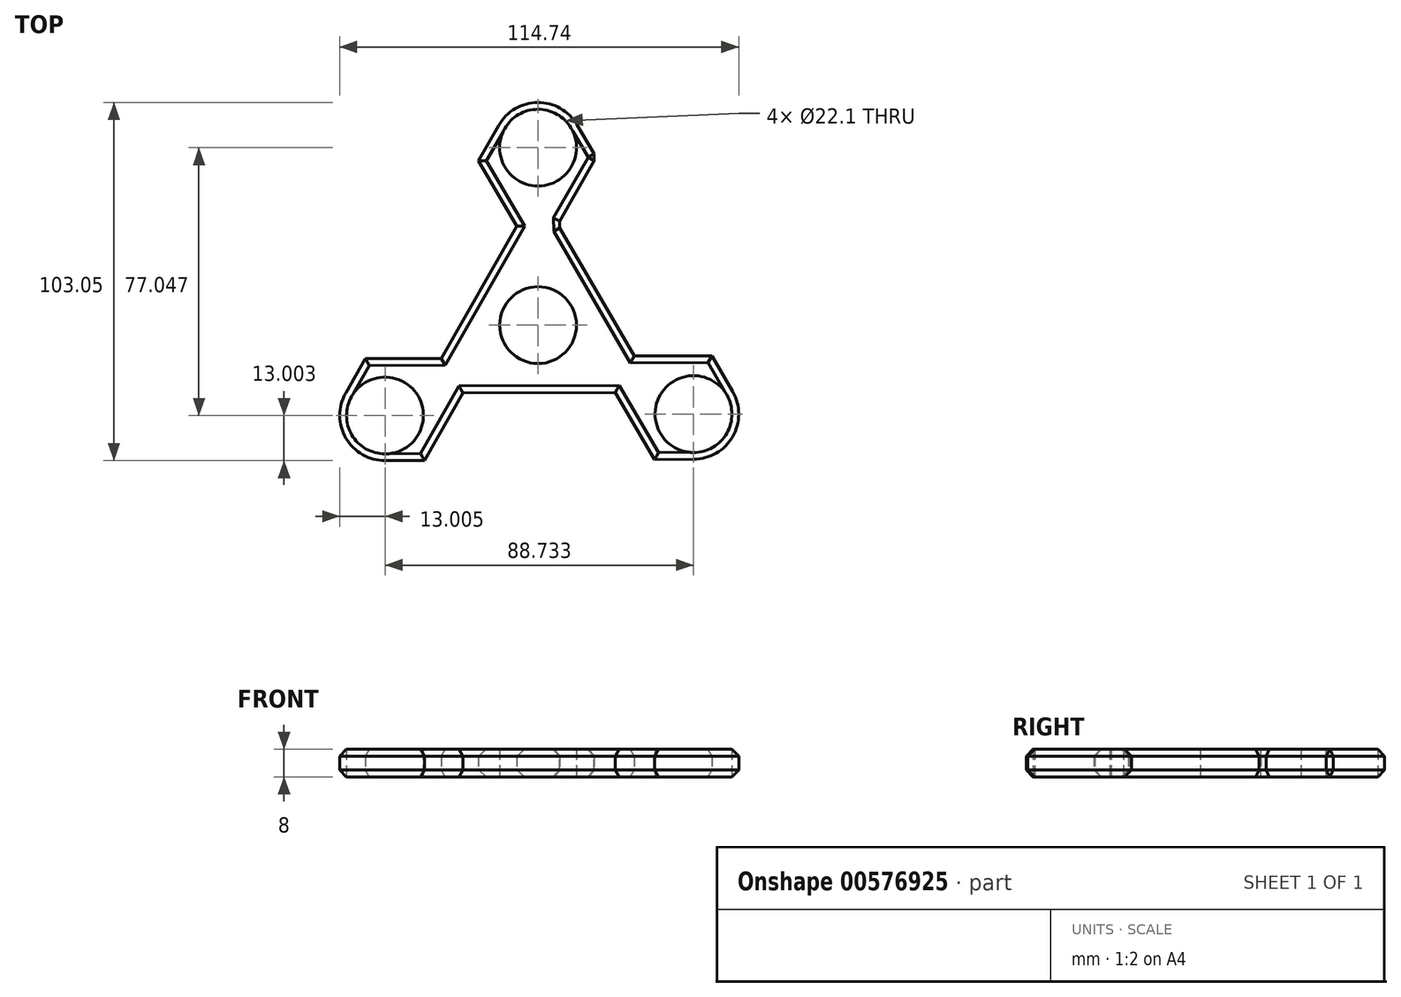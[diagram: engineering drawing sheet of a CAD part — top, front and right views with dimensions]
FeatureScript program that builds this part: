
annotation { "Feature Type Name" : "Feature", "Feature Type Description" : "" }
export const myFeature = defineFeature(function(context is Context, id is Id, definition is map)
    precondition{}
    {
        {
            var Q0;
            Q0=qCreatedBy(makeId("Top.planeOp"),FACE);
            var sketch = newSketch(context, id + "F0", { "sketchPlane" : qUnion([Q0])});
            skCircle(sketch, "E0", {"center": v(0, 0) * mm, "radius": 11.05 * mm});
            skCircle(sketch, "E1", {"center": v(0, 51.05) * mm, "radius": 13 * mm});
            skCircle(sketch, "E2.1.0", {"center": v(-44.02, -26) * mm, "radius": 13 * mm});
            skCircle(sketch, "E2.2.0", {"center": v(44.72, -25.6) * mm, "radius": 13 * mm});
            skPoint(sketch, "E2.center", {"position": v(0.23, -0.18) * mm});
            skLineSegment(sketch, "E3", {"start": v(-55.3, -19.55) * mm, "end": v(-49.66, -9.67) * mm});
            skLineSegment(sketch, "E4", {"start": v(-43.96, -39) * mm, "end": v(-32.66, -38.95) * mm});
            skLineSegment(sketch, "E5", {"start": v(-32.66, -38.95) * mm, "end": v(-21.58, -19.55) * mm});
            skLineSegment(sketch, "E6", {"start": v(-21.58, -19.55) * mm, "end": v(22.22, -19.35) * mm});
            skLineSegment(sketch, "E7", {"start": v(22.22, -19.35) * mm, "end": v(33.48, -38.64) * mm});
            skLineSegment(sketch, "E8.1.0", {"start": v(50.06, -8.8) * mm, "end": v(27.72, -8.91) * mm});
            skLineSegment(sketch, "E8.1.1", {"start": v(27.72, -8.91) * mm, "end": v(5.65, 28.92) * mm});
            skLineSegment(sketch, "E8.1.2", {"start": v(5.65, 28.92) * mm, "end": v(16.73, 48.31) * mm});
            skLineSegment(sketch, "E8.2.0", {"start": v(-17.4, 47.75) * mm, "end": v(-6.14, 28.46) * mm});
            skLineSegment(sketch, "E8.2.1", {"start": v(-6.14, 28.46) * mm, "end": v(-27.87, -9.57) * mm});
            skLineSegment(sketch, "E8.2.2", {"start": v(-27.87, -9.57) * mm, "end": v(-50.2, -9.67) * mm});
            skLineSegment(sketch, "E9.trimOffspring", {"start": v(33.48, -38.64) * mm, "end": v(44.78, -38.6) * mm});
            skLineSegment(sketch, "E10.trimOffspring", {"start": v(-17.12, 47.28) * mm, "end": v(-11.29, 57.5) * mm});
            skLineSegment(sketch, "E11", {"start": v(16.73, 48.31) * mm, "end": v(11.19, 57.67) * mm});
            skLineSegment(sketch, "E12", {"start": v(50.06, -8.8) * mm, "end": v(55.98, -19.1) * mm});
            skCircle(sketch, "E13", {"center": v(0, 51.05) * mm, "radius": 11.05 * mm});
            skCircle(sketch, "E14.1.0", {"center": v(-44.02, -26) * mm, "radius": 11.05 * mm});
            skCircle(sketch, "E14.2.0", {"center": v(44.72, -25.6) * mm, "radius": 11.05 * mm});
            skSolve(sketch);
        }
        {
            var Q0;
            Q0 = qSketchRegion(id + "F0", true);
            extrude(context, id + "F1", {"entities" : qUnion([Q0]), "depth" : 8 * mm, "offsetDistance" : 25 * mm});
        }
        {
            var Q0;
            Q0=makeQuery(id+"F1.opExtrude","CAP_EDGE",EDGE,{"disambiguationData":[OSD([sQuery(id+"F0.wireOp",EDGE,"E8.1.1")])],"isStart":false});
            var Q1;
            Q1=makeQuery(id+"F1.opExtrude","CAP_EDGE",EDGE,{"disambiguationData":[OSD([sQuery(id+"F0.wireOp",EDGE,"E8.1.2")])],"isStart":false});
            var Q2;
            Q2=makeQuery(id+"F1.opExtrude","CAP_EDGE",EDGE,{"disambiguationData":[OSD([sQuery(id+"F0.wireOp",EDGE,"E11")])],"isStart":false});
            var Q3;
            Q3=makeQuery(id+"F1.opExtrude","CAP_EDGE",EDGE,{"disambiguationData":[OSD([sQuery(id+"F0.wireOp",EDGE,"E8.2.0")])],"isStart":false});
            var Q4;
            Q4=makeQuery(id+"F1.opExtrude","CAP_EDGE",EDGE,{"disambiguationData":[OSD([sQuery(id+"F0.wireOp",EDGE,"E8.2.1")])],"isStart":false});
            var Q5;
            Q5=makeQuery(id+"F1.opExtrude","CAP_EDGE",EDGE,{"disambiguationData":[OSD([sQuery(id+"F0.wireOp",EDGE,"E8.2.2")])],"isStart":false});
            var Q6;
            Q6=makeQuery(id+"F1.opExtrude","CAP_EDGE",EDGE,{"disambiguationData":[OSD([sQuery(id+"F0.wireOp",EDGE,"E3")])],"isStart":false});
            var Q7;
            Q7=makeQuery(id+"F1.opExtrude","CAP_EDGE",EDGE,{"disambiguationData":[OSD([sQuery(id+"F0.wireOp",EDGE,"E5")])],"isStart":false});
            var Q8;
            Q8=makeQuery(id+"F1.opExtrude","CAP_EDGE",EDGE,{"disambiguationData":[OSD([sQuery(id+"F0.wireOp",EDGE,"E6")])],"isStart":false});
            var Q9;
            Q9=makeQuery(id+"F1.opExtrude","CAP_EDGE",EDGE,{"disambiguationData":[OSD([sQuery(id+"F0.wireOp",EDGE,"E7")])],"isStart":false});
            var Q10;
            Q10=makeQuery(id+"F1.opExtrude","CAP_EDGE",EDGE,{"disambiguationData":[OSD([sQuery(id+"F0.wireOp",EDGE,"E9.trimOffspring")])],"isStart":false});
            var Q11;
            Q11=makeQuery(id+"F1.opExtrude","CAP_EDGE",EDGE,{"disambiguationData":[OSD([sQuery(id+"F0.wireOp",EDGE,"E8.1.0")])],"isStart":false});
            var Q12;
            Q12=makeQuery(id+"F1.opExtrude","CAP_EDGE",EDGE,{"disambiguationData":[OSD([sQuery(id+"F0.wireOp",EDGE,"E8.1.1")])],"isStart":true});
            var Q13;
            Q13=makeQuery(id+"F1.opExtrude","SWEPT_FACE",FACE,{"disambiguationData":[OSD([sQuery(id+"F0.wireOp",EDGE,"E8.1.2")])]});
            var Q14;
            Q14=makeQuery(id+"F1.opExtrude","CAP_EDGE",EDGE,{"disambiguationData":[OSD([sQuery(id+"F0.wireOp",EDGE,"E11")])],"isStart":true});
            var Q15;
            Q15=makeQuery(id+"F1.opExtrude","CAP_EDGE",EDGE,{"disambiguationData":[OSD([sQuery(id+"F0.wireOp",EDGE,"E8.2.0")])],"isStart":true});
            var Q16;
            Q16=makeQuery(id+"F1.opExtrude","CAP_EDGE",EDGE,{"disambiguationData":[OSD([sQuery(id+"F0.wireOp",EDGE,"E8.2.1")])],"isStart":true});
            var Q17;
            Q17=makeQuery(id+"F1.opExtrude","CAP_EDGE",EDGE,{"disambiguationData":[OSD([sQuery(id+"F0.wireOp",EDGE,"E8.2.2")])],"isStart":true});
            var Q18;
            Q18=makeQuery(id+"F1.opExtrude","CAP_EDGE",EDGE,{"disambiguationData":[OSD([sQuery(id+"F0.wireOp",EDGE,"E3")])],"isStart":true});
            var Q19;
            Q19=makeQuery(id+"F1.opExtrude","CAP_EDGE",EDGE,{"disambiguationData":[OSD([sQuery(id+"F0.wireOp",EDGE,"E5")])],"isStart":true});
            var Q20;
            Q20=makeQuery(id+"F1.opExtrude","CAP_EDGE",EDGE,{"disambiguationData":[OSD([sQuery(id+"F0.wireOp",EDGE,"E6")])],"isStart":true});
            var Q21;
            Q21=makeQuery(id+"F1.opExtrude","CAP_EDGE",EDGE,{"disambiguationData":[OSD([sQuery(id+"F0.wireOp",EDGE,"E7")])],"isStart":true});
            var Q22;
            Q22=makeQuery(id+"F1.opExtrude","CAP_EDGE",EDGE,{"disambiguationData":[OSD([sQuery(id+"F0.wireOp",EDGE,"E2.2.0")])],"isStart":true});
            var Q23;
            Q23=makeQuery(id+"F1.opExtrude","CAP_EDGE",EDGE,{"disambiguationData":[OSD([sQuery(id+"F0.wireOp",EDGE,"E8.1.0")])],"isStart":true});
            chamfer(context, id + "F2", {"entities" : qUnion([Q0, Q1, Q2, Q3, Q4, Q5, Q6, Q7, Q8, Q9, Q10, Q11, Q12, Q13, Q14, Q15, Q16, Q17, Q18, Q19, Q20, Q21, Q22, Q23]), "width" : 2 * mm, "tangentPropagation" : true});
        }
    });
